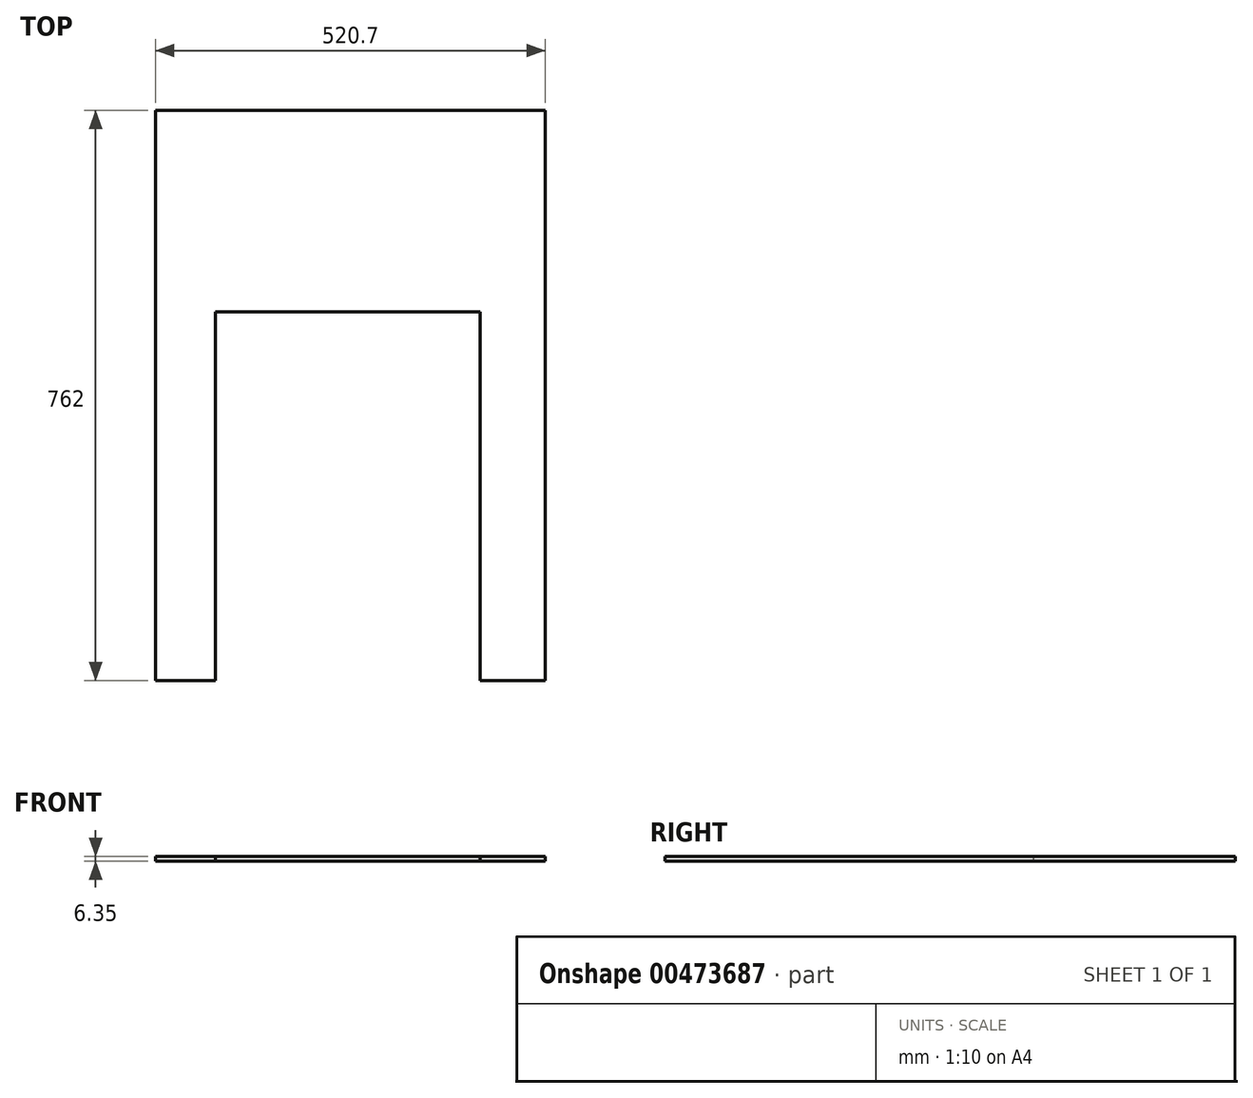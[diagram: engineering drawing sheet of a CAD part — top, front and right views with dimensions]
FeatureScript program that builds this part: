
annotation { "Feature Type Name" : "Feature", "Feature Type Description" : "" }
export const myFeature = defineFeature(function(context is Context, id is Id, definition is map)
    precondition{}
    {
        {
            var Q0;
            Q0=qCreatedBy(makeId("Top.planeOp"),FACE);
            var sketch = newSketch(context, id + "F0", { "sketchPlane" : qUnion([Q0])});
            skLineSegment(sketch, "E0.bottom", {"start": v(260.35, -381) * mm, "end": v(-260.35, -381) * mm});
            skLineSegment(sketch, "E0.top", {"start": v(260.35, 381) * mm, "end": v(-260.35, 381) * mm});
            skLineSegment(sketch, "E0.left", {"start": v(260.35, -381) * mm, "end": v(260.35, 381) * mm});
            skLineSegment(sketch, "E0.right", {"start": v(-260.35, -381) * mm, "end": v(-260.35, 381) * mm});
            skPoint(sketch, "E0.middle", {"position": v(0, 0) * mm});
            skSolve(sketch);
        }
        {
            var Q0;
            Q0=qSketchRegion(id+"F0",true);
            extrude(context, id + "F1", {"entities" : qUnion([Q0]), "depth" : 6.35 * mm});
        }
        {
            var Q0;
            Q0=makeQuery(id+"F1.opExtrude","CAP_FACE",FACE,{"disambiguationData":[OSD([sQuery(id+"F0.wireOp",EDGE,"E0.bottom"),sQuery(id+"F0.wireOp",EDGE,"E0.top"),sQuery(id+"F0.wireOp",EDGE,"E0.left"),sQuery(id+"F0.wireOp",EDGE,"E0.right")])],"isStart":false});
            var sketch = newSketch(context, id + "F2", { "sketchPlane" : qUnion([Q0])});
            skLineSegment(sketch, "E1.bottom", {"start": v(-180.67, -381) * mm, "end": v(173.17, -381) * mm});
            skLineSegment(sketch, "E1.top", {"start": v(-180.67, 111.66) * mm, "end": v(173.17, 111.66) * mm});
            skLineSegment(sketch, "E1.left", {"start": v(-180.67, -381) * mm, "end": v(-180.67, 111.66) * mm});
            skLineSegment(sketch, "E1.right", {"start": v(173.17, -381) * mm, "end": v(173.17, 111.66) * mm});
            skSolve(sketch);
        }
        {
            var Q0;
            Q0=makeQuery(id+"F2.imprint","IMPRINT",FACE,{"disambiguationData":[TD([[makeQuery(id+"F2.imprint","IMPRINT",EDGE,{"derivedFrom":sQuery(id+"F2.wireOp",EDGE,"E1.bottom")}),-1.0]])]});
            extrude(context, id + "F3", {"entities" : qUnion([Q0]), "operationType" : NewBodyOperationType.REMOVE, "oppositeDirection" : true, "depth" : 50.8 * mm});
        }
    });
